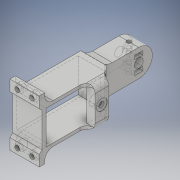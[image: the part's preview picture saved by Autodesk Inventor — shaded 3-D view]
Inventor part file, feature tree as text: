
AUTODESK INVENTOR PART (.ipt)
format: ipt  version: 2019 (Build 230136000, 136)  size: 396,288 bytes
history: native  units: mm
features: sketch x15, extrude x11, hole x4, fillet x4, chamfer x2, plane x2, mirror x2
ambient origin geometry x8: Origin, YZ Plane, XZ Plane, XY Plane, X Axis, Y Axis, Z Axis, Center Point
bodies: Solid1 (feature_tree)
feature tree (40):
  extrude  "Extrusion1"  Depth=29.9mm
  extrude  "Extrusion2"  Depth=10.0mm
  extrude  "Extrusion4"  Depth=5.795264mm
  extrude  "Extrusion5"  Depth=10.0mm
  chamfer  "Chamfer1"  Distance=13.5mm
  extrude  "Extrusion6"  Depth=1.5mm TaperAngle=0.0deg
  extrude  "Extrusion8"  Depth=10.0mm
  hole  "Hole3"  [1 undecoded]
  hole  "Hole4"  [1 undecoded]
  fillet  "Fillet1"  Radius=8.0mm
  fillet  "Fillet2"  Radius=2.95mm
  fillet  "Fillet3"  Radius=6.3mm
  plane  "Work Plane1"
  extrude  "Extrusion9"  Depth=10.1mm
  hole  "Hole5"  [1 undecoded]
  mirror  "Mirror1"
  fillet  "Fillet5"  Radius=10.1mm
  chamfer  "Chamfer2"  Distance=10.5mm
  extrude  "Extrusion10"  [1 undecoded]
  extrude  "Extrusion12"  Depth=2.8mm
  hole  "Hole6"  [1 undecoded]
  plane  "Work Plane3"
  extrude  "Extrusion13"  Depth=2.8mm TaperAngle=0.0deg
  mirror  "Mirror2"
  extrude  "Extrusion14"  Depth=2.8mm
  sketch  "Sketch1"  dims[d0=20.0mm d1=29.9mm]
  sketch  "Sketch3"  dims[d2=3.1mm d3=10.0mm]
  sketch  "Sketch5"  dims[d4=2.95mm d5=5.795264mm]
  sketch  "Sketch6"  dims[d6=10.0mm d7=12.0mm d8=13.5mm d9=0.0mm]
  sketch  "Sketch8"  dims[d19=1.5mm d20=1.5mm d21=0.0mm]
  sketch  "Sketch11"  dims[d26=24.6mm d27=10.0mm]
  sketch  "Sketch12"  dims[d28=45.0mm d29=50.0mm]
  sketch  "Sketch13"  dims[d30=29.1mm d31=10.0mm d32=0.0mm d33=8.0mm d34=0.0mm]
  sketch  "Sketch14"  dims[d35=6.0mm d36=2.0mm d37=45.0deg d38=2.95mm d39=6.3mm]
  sketch  "Sketch15"  dims[d40=6.0mm d41=0.0mm d53=10.1mm]
  sketch  "Sketch16"  dims[d54=10.0mm d55=6.0mm d56=0.0mm d57=10.1mm]
  sketch  "Sketch18"  dims[d58=4.0mm d59=6.0mm d60=8.0mm d61=0.35mm d62=90.0deg d63=10.0mm d64=0.0mm]
  sketch  "Sketch19"  dims[d65=7.0mm d66=6.0mm d67=8.0mm d68=1.0mm d69=90.0deg d70=4.0mm d71=0.0mm]
  sketch  "Sketch20"  dims[d72=5.0mm]
  sketch  "Sketch21"  dims[d73=5.0mm d74=10.5mm d75=-2.0mm d76=8.0mm d77=8.0mm d78=4.0mm d79=0.0mm d81=3.5mm d82=6.0mm d83=6.0mm d84=2.0mm d85=90.0deg d86=8.0mm d87=20.594885mm d88=6.0mm d89=2.0mm d90=2.0mm d91=45.0deg d92=1.0mm d93=0.0mm d99=10.0mm d100=0.0mm d101=3.1mm d102=6.0mm d103=4.0mm d104=2.0mm d105=90.0deg d106=10.0mm d107=0.0mm d108=-5.0mm d109=5.9mm d110=2.8mm d111=0.0mm d112=6.4mm d113=2.8mm d114=0.0mm]
note: 5 required parameter values undecoded (feature->parameter linkage not recoverable at this tier; creation-order binding heuristic only, values carry confidence <= 0.55)
